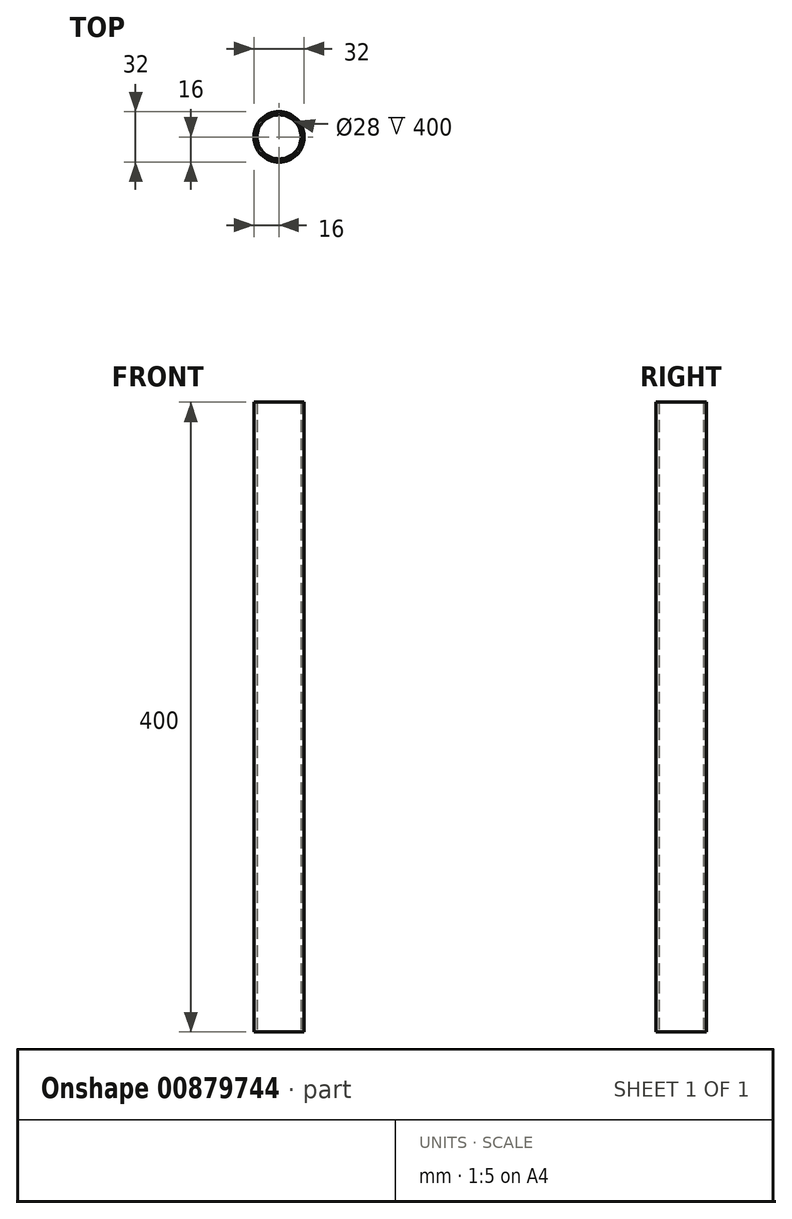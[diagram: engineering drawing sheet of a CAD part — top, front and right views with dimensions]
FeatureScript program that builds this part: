
annotation { "Feature Type Name" : "Feature", "Feature Type Description" : "" }
export const myFeature = defineFeature(function(context is Context, id is Id, definition is map)
    precondition{}
    {
        {
            var Q0;
            Q0=qCreatedBy(makeId("Top.planeOp"),FACE);
            var sketch = newSketch(context, id + "F0", { "sketchPlane" : qUnion([Q0])});
            skCircle(sketch, "E0", {"center": v(0, 0) * mm, "radius": 16 * mm});
            skCircle(sketch, "E1.0", {"center": v(0, 0) * mm, "radius": 14 * mm});
            skSolve(sketch);
        }
        {
            var Q0;
            Q0 = qSketchRegion(id + "F0", true);
            extrude(context, id + "F1", {"entities" : qUnion([Q0]), "depth" : 400 * mm, "offsetDistance" : 25 * mm});
        }
    });
